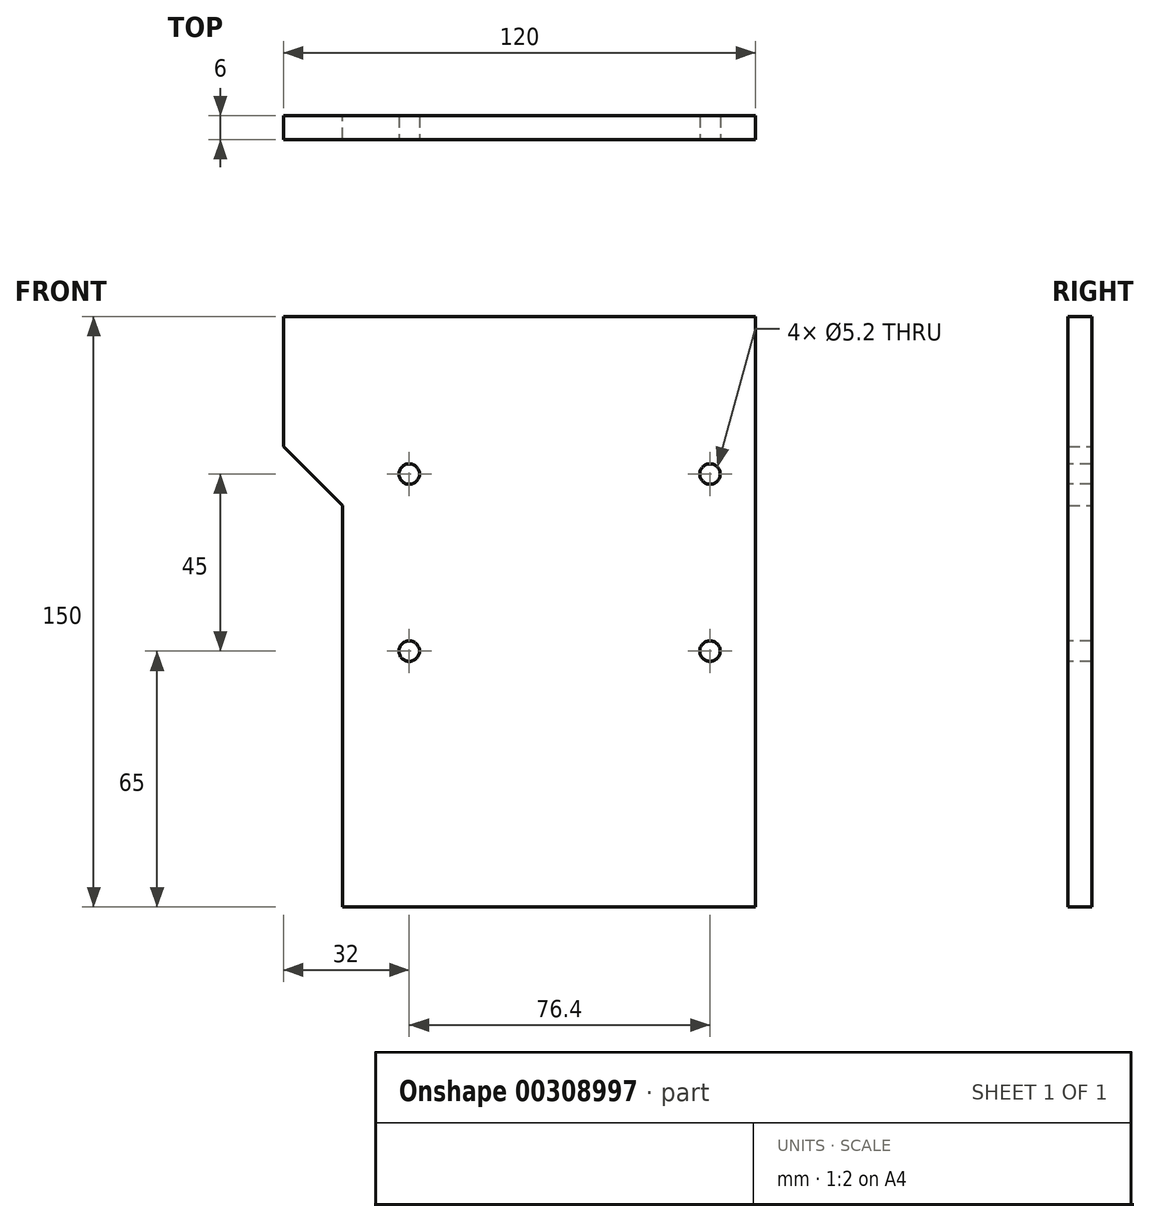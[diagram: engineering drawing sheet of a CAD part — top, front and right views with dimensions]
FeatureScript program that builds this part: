
annotation { "Feature Type Name" : "Feature", "Feature Type Description" : "" }
export const myFeature = defineFeature(function(context is Context, id is Id, definition is map)
    precondition{}
    {
        {
            var Q0;
            Q0=qCreatedBy(makeId("Front.planeOp"),FACE);
            var sketch = newSketch(context, id + "F0", { "sketchPlane" : qUnion([Q0])});
            skLineSegment(sketch, "E0", {"start": v(0, 0) * mm, "end": v(0, 150) * mm});
            skLineSegment(sketch, "E1", {"start": v(0, 150) * mm, "end": v(-120, 150) * mm});
            skLineSegment(sketch, "E2", {"start": v(-120, 150) * mm, "end": v(-120, 117) * mm});
            skLineSegment(sketch, "E3", {"start": v(-120, 117) * mm, "end": v(-105, 102) * mm});
            skLineSegment(sketch, "E4", {"start": v(-105, 102) * mm, "end": v(-105, 0) * mm});
            skLineSegment(sketch, "E5", {"start": v(-105, 0) * mm, "end": v(0, 0) * mm});
            skSolve(sketch);
        }
        {
            var Q0;
            Q0=makeQuery(id+"F0.imprint","IMPRINT",FACE,{"disambiguationData":[TD([[makeQuery(id+"F0.imprint","IMPRINT",EDGE,{"derivedFrom":sQuery(id+"F0.wireOp",EDGE,"E0")}),1.0]])]});
            extrude(context, id + "F1", {"entities" : qUnion([Q0]), "depth" : 6 * mm});
        }
        {
            var Q0;
            Q0=makeQuery(id+"F1.opExtrude","CAP_FACE",FACE,{"disambiguationData":[OSD([sQuery(id+"F0.wireOp",EDGE,"E0"),sQuery(id+"F0.wireOp",EDGE,"E1"),sQuery(id+"F0.wireOp",EDGE,"E2"),sQuery(id+"F0.wireOp",EDGE,"E3"),sQuery(id+"F0.wireOp",EDGE,"E4"),sQuery(id+"F0.wireOp",EDGE,"E5")])],"isStart":false});
            var sketch = newSketch(context, id + "F2", { "sketchPlane" : qUnion([Q0])});
            skLineSegment(sketch, "E6.bottom", {"start": v(-88, 110) * mm, "end": v(-11.6, 110) * mm, "construction": true});
            skLineSegment(sketch, "E6.top", {"start": v(-88, 65) * mm, "end": v(-11.6, 65) * mm, "construction": true});
            skLineSegment(sketch, "E6.left", {"start": v(-88, 110) * mm, "end": v(-88, 65) * mm, "construction": true});
            skLineSegment(sketch, "E6.right", {"start": v(-11.6, 110) * mm, "end": v(-11.6, 65) * mm, "construction": true});
            skPoint(sketch, "E7", {"position": v(-11.6, 110) * mm});
            skPoint(sketch, "E8", {"position": v(-88, 110) * mm});
            skPoint(sketch, "E9", {"position": v(-88, 65) * mm});
            skPoint(sketch, "E10", {"position": v(-11.6, 65) * mm});
            skSolve(sketch);
        }
        {
            var Q0;
            Q0=sQuery(id+"F2.wireOp",VERTEX,"E7");
            var Q1;
            Q1=sQuery(id+"F2.wireOp",VERTEX,"E8");
            var Q2;
            Q2=sQuery(id+"F2.wireOp",VERTEX,"E9");
            var Q3;
            Q3=sQuery(id+"F2.wireOp",VERTEX,"E10");
            var Q4;
            Q4=makeQuery(id+"F1.opExtrude","SWEPT_BODY",BODY,{"disambiguationData":[OSD([sQuery(id+"F0.wireOp",EDGE,"E0"),sQuery(id+"F0.wireOp",EDGE,"E1"),sQuery(id+"F0.wireOp",EDGE,"E2"),sQuery(id+"F0.wireOp",EDGE,"E3"),sQuery(id+"F0.wireOp",EDGE,"E4"),sQuery(id+"F0.wireOp",EDGE,"E5")])]});
            hole(context, id + "F3", {"style" : HoleStyle.SIMPLE, "endStyle" : HoleEndStyle.THROUGH, "holeDiameter" : 5.2 * mm, "tappedDepth" : 12 * mm, "tapClearance" : 3, "locations" : qUnion([Q0, Q1, Q2, Q3]), "scope" : qUnion([Q4])});
        }
    });
